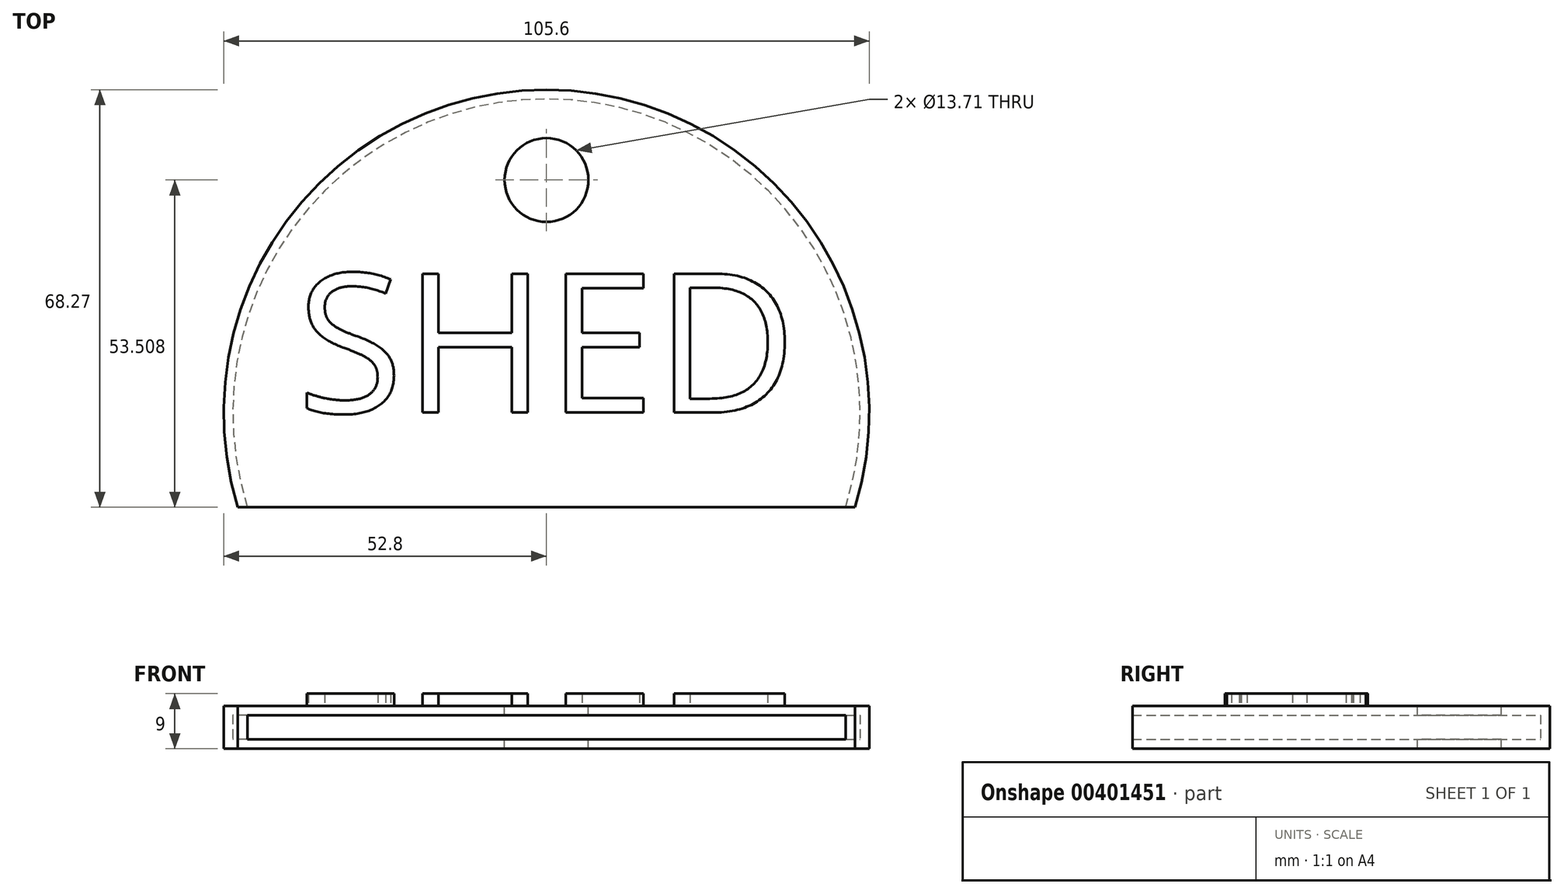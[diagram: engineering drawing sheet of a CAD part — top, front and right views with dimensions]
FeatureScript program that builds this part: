
annotation { "Feature Type Name" : "Feature", "Feature Type Description" : "" }
export const myFeature = defineFeature(function(context is Context, id is Id, definition is map)
    precondition{}
    {
        {
            var Q0;
            Q0=qCreatedBy(makeId("Top.planeOp"),FACE);
            var sketch = newSketch(context, id + "F0", { "sketchPlane" : qUnion([Q0])});
            skArc(sketch, "E0", {"start": v(50.49, -15.47) * mm, "mid": v(0, 52.8) * mm, "end": v(-50.49, -15.47) * mm});
            skLineSegment(sketch, "E1", {"start": v(-50.49, -15.47) * mm, "end": v(50.49, -15.47) * mm});
            skSolve(sketch);
        }
        {
            var Q0;
            Q0=makeQuery(id+"F0.imprint","IMPRINT",FACE,{"disambiguationData":[TD([[makeQuery(id+"F0.imprint","IMPRINT",EDGE,{"derivedFrom":sQuery(id+"F0.wireOp",EDGE,"E0")}),1.0]])]});
            extrude(context, id + "F1", {"entities" : qUnion([Q0]), "endBound" : BoundingType.SYMMETRIC, "depth" : 7 * mm});
        }
        {
            var Q0;
            Q0=makeQuery(id+"F1.opExtrude","SWEPT_FACE",FACE,{"disambiguationData":[OSD([sQuery(id+"F0.wireOp",EDGE,"E1")])]});
            shell(context, id + "F2", {"entities" : qUnion([Q0]), "thickness" : 1.5 * mm});
        }
        {
            var Q0;
            Q0=makeQuery(id+"F1.opExtrude","CAP_FACE",FACE,{"disambiguationData":[OSD([sQuery(id+"F0.wireOp",EDGE,"E0"),sQuery(id+"F0.wireOp",EDGE,"E1")])],"isStart":false});
            var sketch = newSketch(context, id + "F3", { "sketchPlane" : qUnion([Q0])});
            skCircle(sketch, "E2", {"center": v(0, 38.04) * mm, "radius": 6.85 * mm});
            skSolve(sketch);
        }
        {
            var Q0;
            Q0=makeQuery(id+"F3.imprint","IMPRINT",FACE,{"disambiguationData":[TD([[makeQuery(id+"F3.imprint","IMPRINT",EDGE,{"derivedFrom":sQuery(id+"F3.wireOp",EDGE,"E2")}),1.0]])]});
            extrude(context, id + "F4", {"entities" : qUnion([Q0]), "operationType" : NewBodyOperationType.REMOVE, "endBound" : BoundingType.THROUGH_ALL, "oppositeDirection" : true, "depth" : 25 * mm});
        }
        {
            var Q0;
            Q0=makeQuery(id+"F1.opExtrude","CAP_FACE",FACE,{"disambiguationData":[OSD([sQuery(id+"F0.wireOp",EDGE,"E0"),sQuery(id+"F0.wireOp",EDGE,"E1")])],"isStart":false});
            var sketch = newSketch(context, id + "F5", { "sketchPlane" : qUnion([Q0])});
            skPoint(sketch, "E3.middle", {"position": v(0, 0) * mm});
            skText(sketch, "E4", { "text": "SHED", "fontName": "OpenSans-Regular.ttf"});
            const initialGuessF5  = {"E4": [-0.04088, 0, 1, 0, 0.0229]};
            skSetInitialGuess(sketch, initialGuessF5);
            skSolve(sketch);
        }
        {
            var Q0;
            Q0 = qSketchRegion(id + "F5", true);
            extrude(context, id + "F6", {"entities" : qUnion([Q0]), "operationType" : NewBodyOperationType.ADD, "depth" : 2 * mm});
        }
    });
